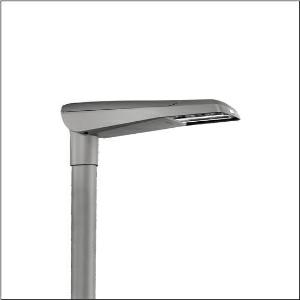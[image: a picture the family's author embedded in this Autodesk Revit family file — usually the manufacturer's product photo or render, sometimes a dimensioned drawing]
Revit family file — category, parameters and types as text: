
# Revit family: streetlight_sl_11_iq_micro___st1_2a_5xc1a41e08ce_a543
name_source: partatom
category: Lighting Fixtures
units: mm (PartAtom-declared; Revit-internal decimal feet)

## family parameters
Cut with Voids When Loaded = No
Host = Face
Light Source = No
Part Type = Normal
Room Calculation Point = No
Round Connector Dimension = Use Diameter
Shared = No

## types (1)
- --- (1 x LED, 1960 lm, 12.6 W, 4000K)
    Apparent Load = 13 VA
    CIE Flux Codes = 33 71 96 100 100
    Color Rendering = 70
    Color Temperature = 4000K
    Default Elevation = 1800 mm
    Description = Streetlight SL 11 iQ micro, mast luminaire, primary light control with 3 zone facetted reflector, of plastic, silver coated, highly specular, primary optical cover: cover, of PMMA, transparent, light distribution: ST1.2a, light emission: direct distribution, primary light characteristic: asymmetric, installation type: post-top, side-entry, lamps: LED, High Power LED, rated values: 1.960lm | 12,6W | 155,6lm/W (begin service life); end service life: 1.960lm | 12,9W; at 50% lumin. flux: 980lm | 6,8W | 144,1lm/W, colour temperature: 4000K, colour rendering: CRI > 70, light colour: 740, light setting 1 begin service life: 100% | 1.960lm | 12,6W | 155,6lm/W | 4.000K, light setting 1 end service life: 12,9W, further light settings possible, control: optimised constant luminous flux control (CLO 2.0), Desk-Remote (wireless, voltage-free reading and setting of iQ features in the workshop via application-optimized NFC function/RFID function), Light-Fading, Smart-Wire, Night-Set, Lumen-Switch, Temp-Guard, Auto-Match, with cable H07RN-F 3x 1.5mm², mains connection: 230..240V, AC, 50/60Hz, connection cable pre-assembled, cable length: 5,5m, luminaire housing, of diecast aluminium, powder-coated, SITECO metallic grey (DB 702S), please order mast flange separately, inclination adjustable without tools: 0°, 5°, 10°, 15° (post-top) | 0°, -5°, -10°, -15° (side-entry), sealing non-destructively replaceable, multi-level sealing system, length: 600mm, width: 174mm, height: 116mm, mast flange for spigot size: 42mm (side-entry): 5XC10008XM4, 60/48mm (side-entry/post-top): 5XC10108XM2, 76/60mm (side-entry/post-top): 5XC10108XM1, equipment: standard, protection rating (complete): IP66, insulation class (complete): insulation class II (safety insulation), certification: CE, ENEC, ENEC+, VDE, impact resistance: IK10, permissible operating ambient temperature for outdoor applications: -25..+50°C, standard-compliant lighting for roads and squares, Environmental Product Declaration (EPD) tested and certified by an independent institute, packaging unit: 1 piece

Light Distribution: ST1.2a
    Height = 116 mm
    Lamp = 1 x LED
    Lamp Light Flux = 1960 lm
    Lamp Power = 12.6 W
    Lamp count = 1
    Length = 600 mm
    Luminous efficacy = 156 lm/W
    Manufacturer = Siteco
    ModVariant = No
    Model = 5XC1A41E08CE
    Mounting Place = Pole
    Mounting Type = Pole top
    Number of Poles = 1
    OnlyDefault = Yes
    Power Factor = 1
    Product Name = Streetlight SL 11 iQ micro | ST1.2a
    Product group = mast luminaire | pylon top
    ProductGroupID = 6100
    Protection Class = Protection class II
    Protection Degree = IP 66
    RLX_Detail_Level = 1
    RLX_Emergency_Light_Flux = 0 lm
    RLX_Emergency_Type = 0
    RLX_Emergency_Type_DB = No
    RlxData = <blob elided: 26505 chars, md5=661356fb>
    Socket = socket
    Standby Power = 0 W
    System Light Flux = 1960 lm
    System Power = 13 W
    Type Comments = factory setting: luminous flux: 100 % | dim-lin: 254 | 229 mA
    Type Image = l_1006566.jpg
    URL = http://relux.com
    VarID = @adj_020771
    Voltage = 0 V
    Weight = 0.00 kg
    Width = 174 mm

## geometry (parser evidence)
native form markers: Blend x4, Sweep x12
no freeform markers — native parametric forms only
